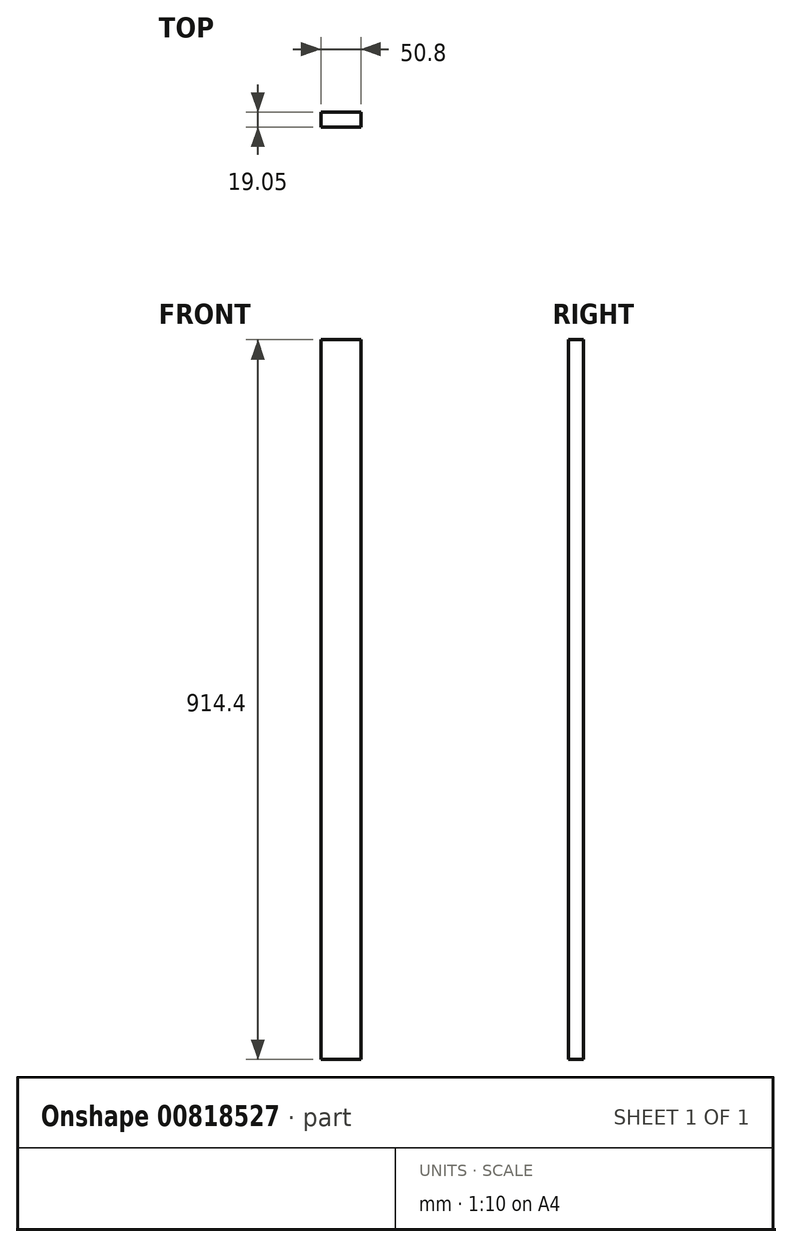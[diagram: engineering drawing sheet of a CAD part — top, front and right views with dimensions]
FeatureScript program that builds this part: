
annotation { "Feature Type Name" : "Feature", "Feature Type Description" : "" }
export const myFeature = defineFeature(function(context is Context, id is Id, definition is map)
    precondition{}
    {
        {
            var Q0;
            Q0=qCreatedBy(makeId("Top.planeOp"),FACE);
            var sketch = newSketch(context, id + "F0", { "sketchPlane" : qUnion([Q0])});
            skLineSegment(sketch, "E0.bottom", {"start": v(44.72, 0) * mm, "end": v(95.52, 0) * mm});
            skLineSegment(sketch, "E0.top", {"start": v(44.72, -19.05) * mm, "end": v(95.52, -19.05) * mm});
            skLineSegment(sketch, "E0.left", {"start": v(44.72, 0) * mm, "end": v(44.72, -19.05) * mm});
            skLineSegment(sketch, "E0.right", {"start": v(95.52, 0) * mm, "end": v(95.52, -19.05) * mm});
            skSolve(sketch);
        }
        {
            var Q0;
            Q0=makeQuery(id+"F0.imprint","IMPRINT",FACE,{"disambiguationData":[TD([[makeQuery(id+"F0.imprint","IMPRINT",EDGE,{"derivedFrom":sQuery(id+"F0.wireOp",EDGE,"E0.bottom")}),-1.0]])]});
            extrude(context, id + "F1", {"entities" : qUnion([Q0]), "depth" : 914.4 * mm, "offsetDistance" : 25.4 * mm});
        }
    });
